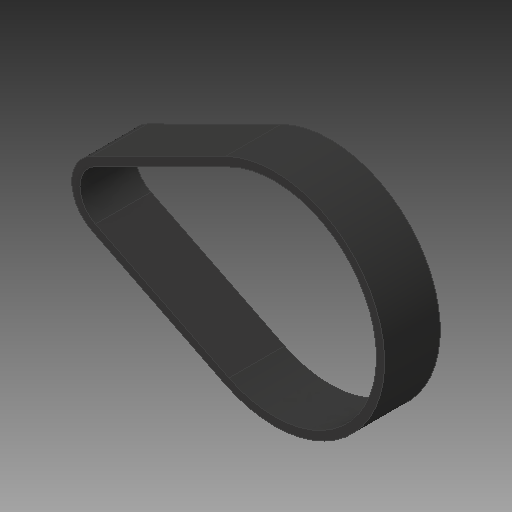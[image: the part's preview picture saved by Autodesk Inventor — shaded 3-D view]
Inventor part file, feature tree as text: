
AUTODESK INVENTOR PART (.ipt)
format: ipt  version: 2019.3 (Build 233278000, 278)  size: 113,152 bytes
history: native  units: mm
features: extrude x1, sketch x1
ambient origin geometry x8: Origin, YZ Plane, XZ Plane, XY Plane, X Axis, Y Axis, Z Axis, Center Point
bodies: Solid1 (feature_tree)
feature tree (2):
  extrude  "Extrusion1"  Depth=45.0mm
  sketch  "Sketch1"  dims[d0=16.434mm d1=45.0mm d3=1.5mm d4=56.54mm d5=0.7mm d6=0.7mm d7=1.5mm d8=15.0mm d9=0.0mm]
